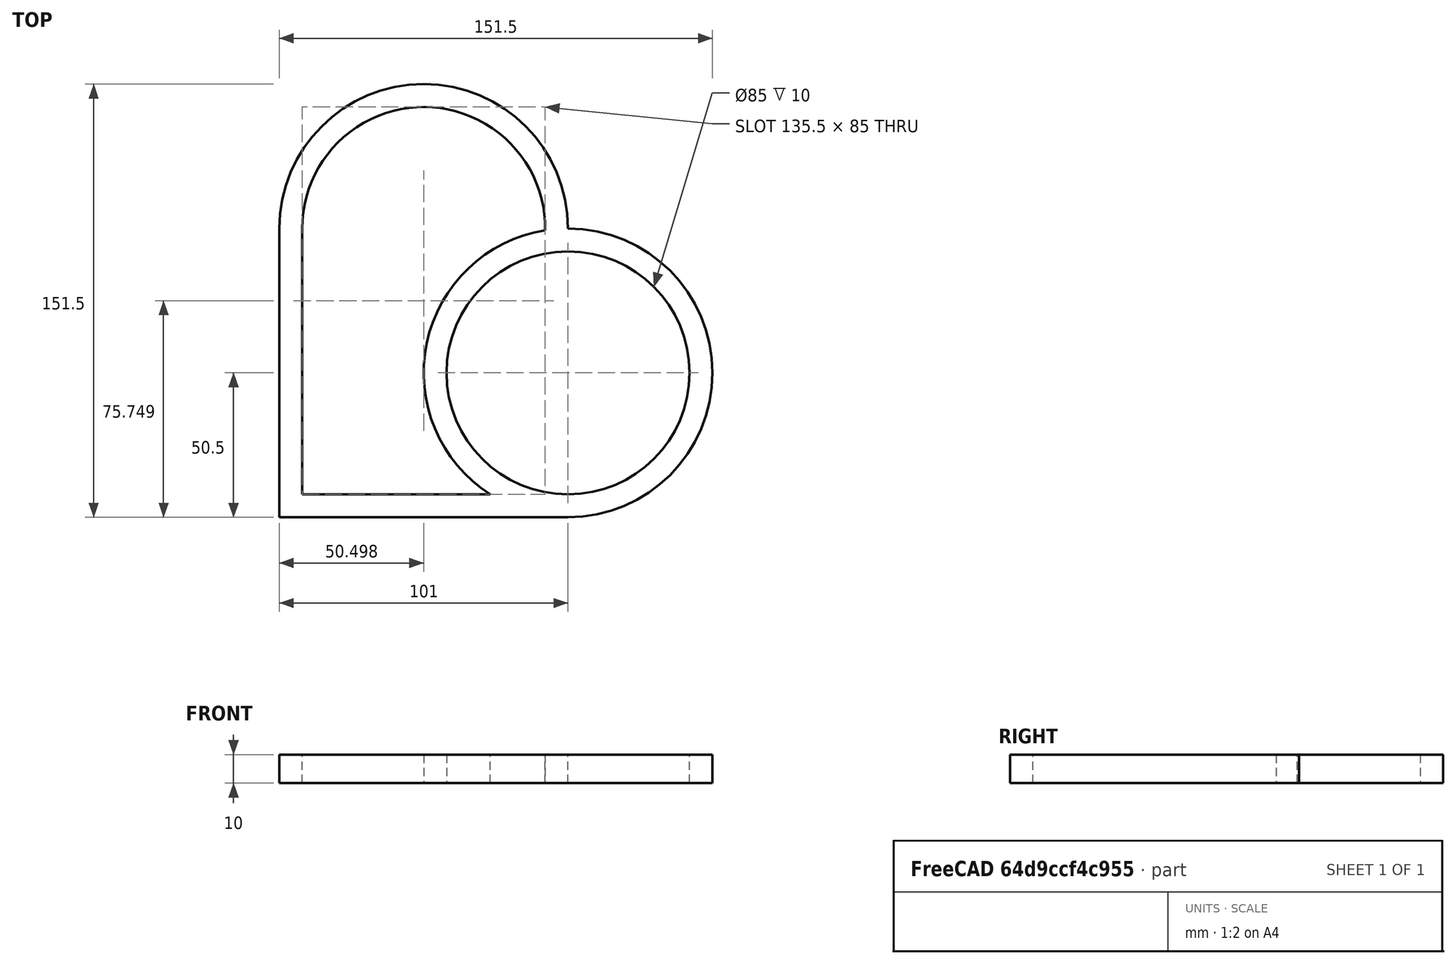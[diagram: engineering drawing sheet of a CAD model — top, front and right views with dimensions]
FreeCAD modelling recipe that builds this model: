
FCSTD DOCUMENT  (FreeCAD 1.0R39109 (Git))
Label: Snacktray mit Tass
License: All rights reserved
LicenseURL: http://en.wikipedia.org/wiki/All_rights_reserved
objects: Sketcher::SketchObject×2, PartDesign::Body×2, PartDesign::Pad×1
note: 9 computed .brp shape members not serialized (recipe doc carries the construction recipe); baked Part::Feature solids carry a one-line shape summary decoded from their .brp

FEATURE [Sketcher::SketchObject] Sketch
  ArcFitTolerance = 1e-06
  AttachmentSupport = -> [XY_Plane]
  FullyConstrained = false
  MakeInternals = false
  MapMode = 5
  sketch-geometry (11):
    g0: LineSegment StartX=-101 StartY=0 StartZ=0 EndX=-101 EndY=-101 EndZ=0
    g1: LineSegment StartX=-101 StartY=-101 StartZ=0 EndX=-1.42e-14 EndY=-101 EndZ=0
    g2: GeomPoint [constr] X=-50.5 Y=0 Z=0
    g3: GeomPoint [constr] X=0 Y=-50.5 Z=0
    g4: ArcOfCircle CenterX=-50.5 CenterY=0 CenterZ=0 NormalX=0 NormalY=0 NormalZ=1 AngleXU=0 Radius=50.5 StartAngle=0 EndAngle=3.14159
    g5: ArcOfCircle CenterX=0 CenterY=-50.5 CenterZ=0 NormalX=0 NormalY=0 NormalZ=1 AngleXU=0 Radius=50.5 StartAngle=4.71239 EndAngle=7.85398
    g6: Circle CenterX=0 CenterY=-50.5 CenterZ=0 NormalX=0 NormalY=0 NormalZ=1 AngleXU=0 Radius=42.5
    g7: ArcOfCircle CenterX=0 CenterY=-50.5 CenterZ=0 NormalX=0 NormalY=0 NormalZ=1 AngleXU=0 Radius=50.5 StartAngle=1.72998 EndAngle=4.1418
    g8: ArcOfCircle CenterX=-50.5 CenterY=0 CenterZ=0 NormalX=0 NormalY=0 NormalZ=1 AngleXU=0 Radius=42.5 StartAngle=6.26816 EndAngle=9.42478
    g9: LineSegment StartX=-93 StartY=0 StartZ=0 EndX=-93 EndY=-93 EndZ=0
    g10: LineSegment StartX=-93 StartY=-93 StartZ=0 EndX=-27.2764 EndY=-93 EndZ=0
  constraints (21):
    c: Coincident(g0,g1)
    c: Horizontal(g1)
    c: Vertical(g0)
    c: Coincident(g4,g2)
    c: Coincident(g5,g3)
    c: Coincident(g5,g4)
    c: PointOnObject(g4,g0)
    c: Coincident(g5,g1)
    c: Diameter(g6) = 85
    c: Coincident(g6,g3)
    c: Diameter(g7) = 101
    c: Coincident(g7,g3)
    c: Diameter(g8) = 85
    c: Coincident(g8,g2)
    c: Coincident(g8,g7)
    c: Coincident(g9,g10)
    c: Horizontal(g10)
    c: Vertical(g9)
    c: Distance(g9,g4) = 93
    c: PointOnObject(g8,g9)
    c: Coincident(g7,g10)
FEATURE [PartDesign::Pad] Pad
  Direction = (0,0,1)
  Length = 10
  Length2 = 10
  Profile = -> Sketch
  ReferenceAxis = -> Sketch [N_Axis]
  Refine = true
  Suppressed = false
  Type = 0
FEATURE [PartDesign::Body] Body  label="Körper"
  AllowCompound = false
  Group = -> [Sketch,Pad]
  Origin = -> Origin
  Tip = -> Pad
FEATURE [Sketcher::SketchObject] Sketch001
  ArcFitTolerance = 1e-06
  AttachmentSupport = -> [XY_Plane001]
  FullyConstrained = false
  MakeInternals = false
  MapMode = 5
  sketch-geometry (6):
    g0: ArcOfCircle CenterX=-50.4036 CenterY=0.0246751 CenterZ=0 NormalX=0 NormalY=0 NormalZ=1 AngleXU=0 Radius=40.9646 StartAngle=0.0160408 EndAngle=3.14225
    g1: ArcOfCircle CenterX=-39.0727 CenterY=-88.5843 CenterZ=0 NormalX=0 NormalY=0 NormalZ=1 AngleXU=0 Radius=3 StartAngle=4.69254 EndAngle=7.05849
    g2: ArcOfCircle CenterX=-88.3682 CenterY=-88.5837 CenterZ=0 NormalX=0 NormalY=0 NormalZ=1 AngleXU=0 Radius=3 StartAngle=3.14159 EndAngle=4.71239
    g3: LineSegment StartX=-91.3682 StartY=-88.5837 StartZ=0 EndX=-91.3682 EndY=0.0517949 EndZ=0
    g4: LineSegment StartX=-88.3682 StartY=-91.5837 StartZ=0 EndX=-39.1323 EndY=-91.5837 EndZ=0
    g5: ArcOfCircle CenterX=0.061564 CenterY=-50.2323 CenterZ=0 NormalX=0 NormalY=0 NormalZ=1 AngleXU=0 Radius=51.7938 StartAngle=1.75537 EndAngle=3.9169
  constraints (11):
    c: Diameter(g1) = 6
    c: Diameter(g2) = 6
    c: PointOnObject(g3,g0)
    c: Vertical(g3)
    c: Horizontal(g4)
    c: Coincident(g0,g5)
    c: PointOnObject(g0,g3)
    c: Tangent(g2,g4) = -1.5708
    c: Tangent(g2,g3) = 1.5708
    c: Tangent(g1,g5) = 1.5708
    c: Coincident(g1,g4)
FEATURE [PartDesign::Body] Body001  label="Körper001"
  AllowCompound = false
  Group = -> [Sketch001]
  Origin = -> Origin001
